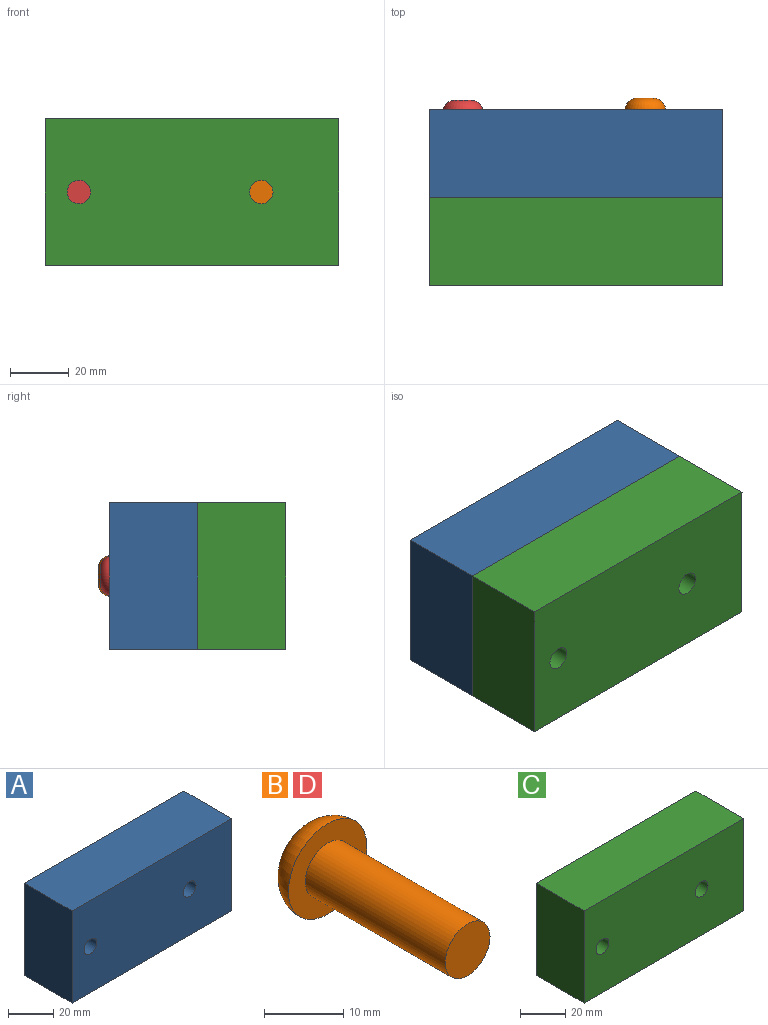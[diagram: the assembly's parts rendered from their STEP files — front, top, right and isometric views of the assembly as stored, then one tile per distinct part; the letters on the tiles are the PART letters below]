
ASSEMBLY  parts=4 mates=4
PART A: 8 faces, bbox 100x30x50 mm
  f0: plane 50x30mm, normal (-1,0,0), area 1500mm2, adj f1,f5,f6,f7
  f1: plane 100x30mm, normal (0,0,-1), area 3000mm2, adj f0,f2,f6,f7
  f2: plane 50x30mm, normal (1,0,0), area 1500mm2, adj f1,f5,f6,f7
  f3: cylinder r=4mm len=30mm, axis (0,1,0), area 754mm2, adj f6,f7
  f4: cylinder r=4mm len=30mm, axis (0,1,0), area 754mm2, adj f6,f7
  f5: plane 100x30mm, normal (0,0,1), area 3000mm2, adj f0,f2,f6,f7
  f6: plane 100x50mm, normal (0,-1,0), area 4899.5mm2, adj f0,f1,f2,f3,f4,f5
  f7: plane 100x50mm, normal (0,1,0), area 4899.5mm2, adj f0,f1,f2,f3,f4,f5
PART B: 12 faces, bbox 14x29.4x14 mm
  f0: plane 7x7mm, normal (0,1,0), area 16.8mm2, adj f3,f5,f6,f7,f8,f9,f10
  f1: cylinder r=4mm len=25mm, axis (0,1,0), area 628.3mm2, adj f2,f4
  f2: plane 8x8mm, normal (0,-1,0), area 50.3mm2, adj f1
  f3: torus R=2.48mm, axis (0,1,0), area 219.6mm2, adj f0,f4
  f4: plane 14x14mm, normal (0,-1,0), area 103.7mm2, adj f1,f3
  f5: plane 4x2.5mm, normal (-0.5,0,0.87), area 11.5mm2, adj f0,f6,f10,f11
  f6: plane 4x2.5mm, normal (0.5,0,0.87), area 11.5mm2, adj f0,f5,f7,f11
  f7: plane 4x2.89mm, normal (1,0,0), area 11.5mm2, adj f0,f6,f8,f11
  f8: plane 4x2.5mm, normal (0.5,0,-0.87), area 11.5mm2, adj f0,f7,f9,f11
  f9: plane 4x2.5mm, normal (-0.5,0,-0.87), area 11.5mm2, adj f0,f8,f10,f11
  f10: plane 4x2.89mm, normal (-1,0,0), area 11.5mm2, adj f0,f5,f9,f11
  f11: plane 5.77x5mm, normal (0,1,0), area 21.7mm2, adj f5,f6,f7,f8,f9,f10
PART C: 8 faces, bbox 100x30x50 mm
  f0: plane 50x30mm, normal (-1,0,0), area 1500mm2, adj f1,f5,f6,f7
  f1: plane 100x30mm, normal (0,0,-1), area 3000mm2, adj f0,f2,f6,f7
  f2: plane 50x30mm, normal (1,0,0), area 1500mm2, adj f1,f5,f6,f7
  f3: cylinder r=4mm len=30mm, axis (0,1,0), area 754mm2, adj f6,f7
  f4: cylinder r=4mm len=30mm, axis (0,1,0), area 754mm2, adj f6,f7
  f5: plane 100x30mm, normal (0,0,1), area 3000mm2, adj f0,f2,f6,f7
  f6: plane 100x50mm, normal (0,-1,0), area 4899.5mm2, adj f0,f1,f2,f3,f4,f5
  f7: plane 100x50mm, normal (0,1,0), area 4899.5mm2, adj f0,f1,f2,f3,f4,f5
PART D: same geometry as B
PLACE A rot(axis=(0,1,0),0deg) t=(-29.76,-149.71,-146.94)mm
PLACE B t=(-84.93,-150.3,-155.12)mm
PLACE C rot(axis=(0,1,0),0deg) t=(-142.95,-179.71,-130.69)mm
PLACE D rot(axis=(0,1,0),0deg) t=(-147.08,-151.01,-155.12)mm
MATE fastened A.f6 <-> C.f7  axis (0,-1,0) through (-108.39,-179.71,-155.12)mm
MATE cylindrical B.f1 <-> A.f4  axis (0,1,0) through (-84.93,-175.3,-155.12)mm
MATE cylindrical A.f4 <-> A.f5  axis (0,1,0) through (-84.93,-149.71,-155.12)mm
MATE cylindrical D.f1 <-> A.f3  axis (0,-1,0) through (-147.08,-151.01,-155.12)mm
